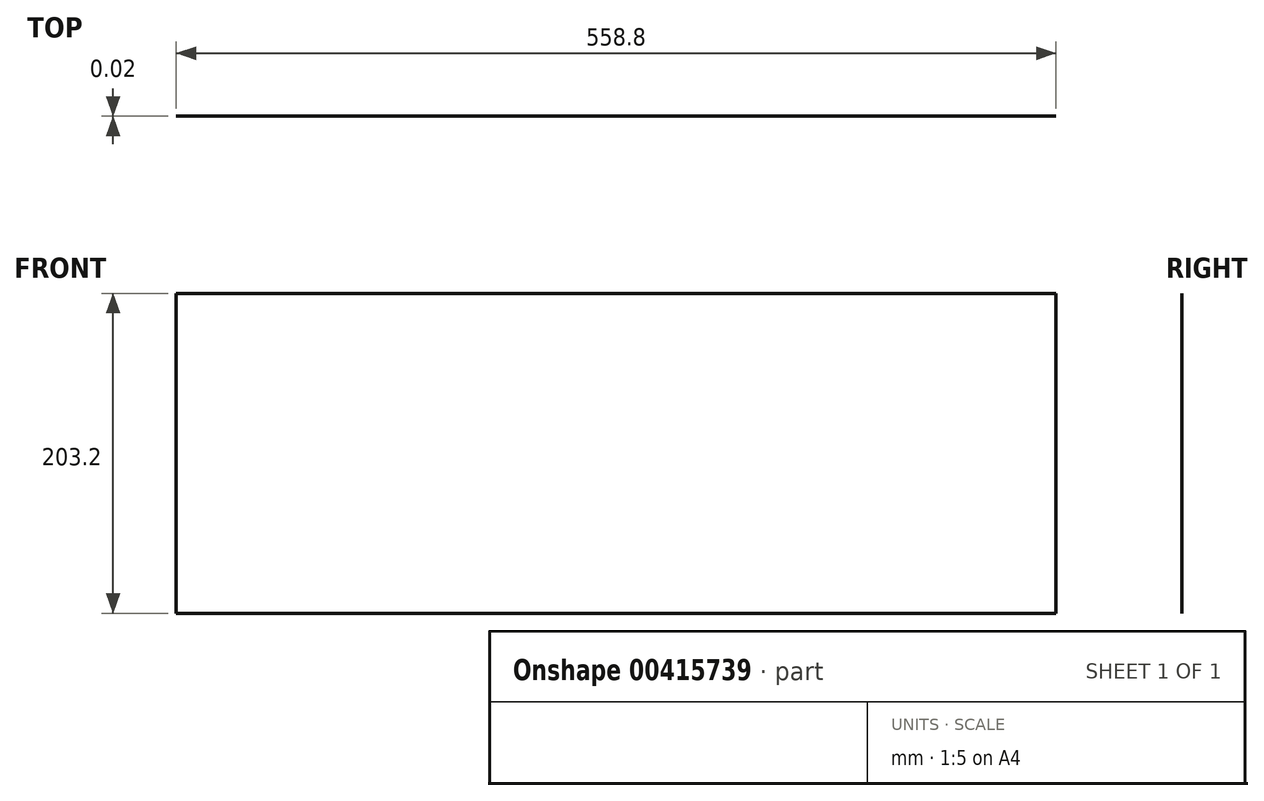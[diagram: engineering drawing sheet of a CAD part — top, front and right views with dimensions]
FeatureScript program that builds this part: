
annotation { "Feature Type Name" : "Feature", "Feature Type Description" : "" }
export const myFeature = defineFeature(function(context is Context, id is Id, definition is map)
    precondition{}
    {
        {
            var Q0;
            Q0=qCreatedBy(makeId("Front.planeOp"),FACE);
            var sketch = newSketch(context, id + "F0", { "sketchPlane" : qUnion([Q0])});
            skLineSegment(sketch, "E0.bottom", {"start": v(279.4, -101.6) * mm, "end": v(-279.4, -101.6) * mm});
            skLineSegment(sketch, "E0.top", {"start": v(279.4, 101.6) * mm, "end": v(-279.4, 101.6) * mm});
            skLineSegment(sketch, "E0.left", {"start": v(279.4, -101.6) * mm, "end": v(279.4, 101.6) * mm});
            skLineSegment(sketch, "E0.right", {"start": v(-279.4, -101.6) * mm, "end": v(-279.4, 101.6) * mm});
            skPoint(sketch, "E0.middle", {"position": v(0, 0) * mm});
            skSolve(sketch);
        }
        {
            var Q0;
            Q0=makeQuery(id+"F0.imprint","IMPRINT",FACE,{"disambiguationData":[TD([[makeQuery(id+"F0.imprint","IMPRINT",EDGE,{"derivedFrom":sQuery(id+"F0.wireOp",EDGE,"E0.bottom")}),-1.0]])]});
            extrude(context, id + "F1", {"entities" : qUnion([Q0]), "depth" : 1 / 50.8 * mm});
        }
    });
